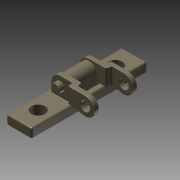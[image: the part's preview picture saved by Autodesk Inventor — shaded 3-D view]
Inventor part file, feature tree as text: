
AUTODESK INVENTOR PART (.ipt)
format: ipt  version: 2013 (Build 170138000, 138)  size: 444,928 bytes
history: native  units: in
note: dims shown in document units (in); Inventor stores cm internally (conversion verified against a paired STEP export)
features: sketch x10, extrude x9, fillet x9, plane x7, mirror x2, hole x1
ambient origin geometry x8: Origin, YZ Plane, XZ Plane, XY Plane, X Axis, Y Axis, Z Axis, Center Point
bodies: Solid1 (feature_tree)
feature tree (38):
  extrude  "Extrusion1"  Depth=0.327in
  plane  "Work Plane1"
  fillet  "Fillet1"  Radius=0.125in
  extrude  "Extrusion2"  Depth=0.315in TaperAngle=0.0deg
  plane  "Work Plane2"
  extrude  "Extrusion4"  Depth=0.236in
  plane  "Work Plane3"
  extrude  "Extrusion7"  Depth=0.087in
  extrude  "Extrusion9"  Depth=0.063in
  fillet  "Fillet5"  Radius=0.0021in
  fillet  "Fillet6"  Radius=0.163in
  fillet  "Fillet7"  Radius=0.0457in
  hole  "Hole1"  [1 undecoded]
  fillet  "Fillet8"  Radius=0.6205in
  fillet  "Fillet9"  Radius=0.6205in
  plane  "Work Plane4"
  mirror  "Mirror1"
  fillet  "Fillet10"  Radius=0.098in
  extrude  "Extrusion10"  Depth=0.386in
  extrude  "Extrusion11"  Depth=0.063in TaperAngle=0.0deg
  fillet  "Fillet11"  Radius=0.02in
  extrude  "Extrusion12"  Depth=0.008in
  plane  "Work Plane7"
  extrude  "Extrusion13"  Depth=0.008in
  fillet  "Fillet12"  Radius=0.079in
  mirror  "Mirror2"
  sketch  "Sketch1"  dims[d0=1.496in d1=0.327in d2=0.125in d3=0.0in]
  sketch  "Sketch2"  dims[d4=0.02in d5=0.315in d6=0.0in]
  sketch  "Sketch6"  dims[d10=0.244in d11=0.236in]
  sketch  "Sketch10"  dims[d12=0.224in d13=0.087in]
  sketch  "Sketch11"  dims[d15=0.059in d16=0.0in d17=0.063in d27=0.0021in d28=0.163in d29=0.0457in]
  sketch  "Sketch13"  dims[d30=0.163in d31=0.1262in d32=0.6205in d33=0.6205in d34=0.098in]
  plane  "Work Plane5"
  plane  "Work Plane6"
  sketch  "Sketch14"  dims[d35=0.118in d38=0.386in]
  sketch  "Sketch15"  dims[d39=0.063in d40=0.059in d41=0.0in d42=0.0in d49=0.063in d50=0.0in d51=0.02in d52=0.02in]
  sketch  "Sketch16"  dims[d53=0.008in d54=0.008in]
  sketch  "Sketch17"  dims[d55=0.122in d56=0.75in d57=0.375in d58=0.25in d59=0.5635in d60=1.0in d61=0.8108in d62=0.008in d63=0.079in d64=0.02in d65=0.063in d66=0.0in d67=0.1571in d68=0.1571in d69=0.258in d70=-0.0034in d71=0.02in d72=0.118in d73=0.066in d74=0.0in d75=0.0392in d76=0.066in d77=0.0in d78=0.008in]
note: 1 required parameter value undecoded (feature->parameter linkage not recoverable at this tier; creation-order binding heuristic only, values carry confidence <= 0.55)
